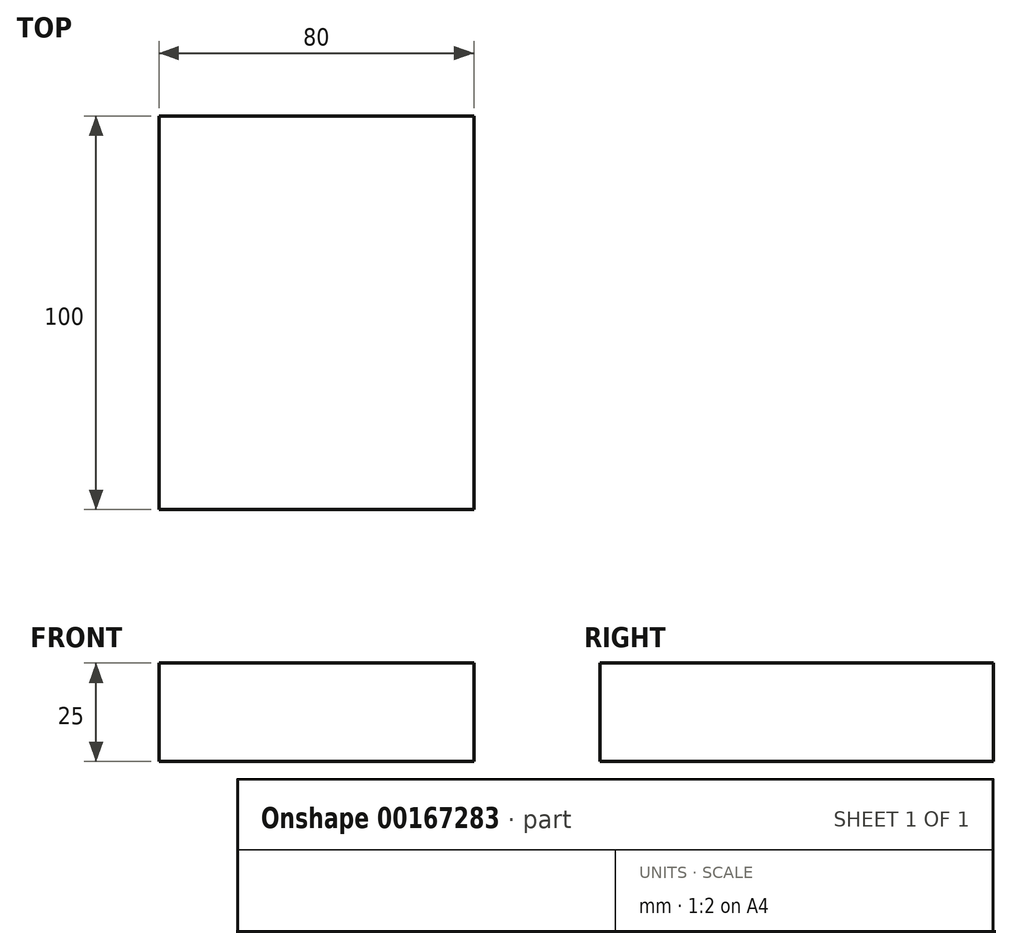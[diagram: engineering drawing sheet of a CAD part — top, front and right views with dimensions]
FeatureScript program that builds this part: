
annotation { "Feature Type Name" : "Feature", "Feature Type Description" : "" }
export const myFeature = defineFeature(function(context is Context, id is Id, definition is map)
    precondition{}
    {
        {
            var Q0;
            Q0=qCreatedBy(makeId("Top.planeOp"),FACE);
            var sketch = newSketch(context, id + "F0", { "sketchPlane" : qUnion([Q0])});
            skLineSegment(sketch, "E0", {"start": v(12.34, 0) * mm, "end": v(92.34, 0) * mm});
            skLineSegment(sketch, "E1", {"start": v(92.34, 0) * mm, "end": v(92.34, 100) * mm});
            skLineSegment(sketch, "E2", {"start": v(92.34, 100) * mm, "end": v(12.34, 100) * mm});
            skLineSegment(sketch, "E3", {"start": v(12.34, 100) * mm, "end": v(12.34, 0) * mm});
            skSolve(sketch);
        }
        {
            var Q0;
            Q0=makeQuery(id+"F0.imprint","IMPRINT",FACE,{"disambiguationData":[TD([[makeQuery(id+"F0.imprint","IMPRINT",EDGE,{"derivedFrom":sQuery(id+"F0.wireOp",EDGE,"E0")}),1.0]])]});
            extrude(context, id + "F1", {"entities" : qUnion([Q0]), "endBound" : BoundingType.SYMMETRIC, "depth" : 25 * mm});
        }
    });
